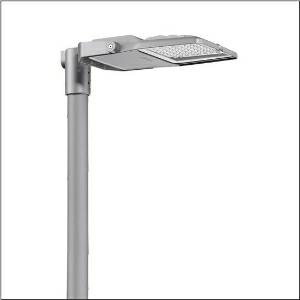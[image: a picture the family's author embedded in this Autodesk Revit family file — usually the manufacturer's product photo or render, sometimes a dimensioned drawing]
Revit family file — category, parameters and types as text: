
# Revit family: floodlight_fl_21_iq_mini___pl64_5xa7771c4e3a_84b6
name_source: partatom
category: Lighting Fixtures
units: mm (PartAtom-declared; Revit-internal decimal feet)

## family parameters
Cut with Voids When Loaded = No
Host = Face
Light Source = No
Part Type = Normal
Room Calculation Point = No
Round Connector Dimension = Use Diameter
Shared = No

## types (1)
- --- (1 x LED, 12280 lm, 87.2 W, 4000K)
    Apparent Load = 87 VA
    CIE Flux Codes = 28 80 98 100 100
    Color Rendering = 70
    Color Temperature = 4000K
    Default Elevation = 1800 mm
    Description = Floodlight FL 21 iQ mini, floodlight, primary light control with lens, of PMMA, primary optical cover: protective disc, of toughened safety glass, transparent, light distribution: PL64, light emission: direct distribution, installation type: surface-mounted, LED, High Power LED, rated luminous flux: 12.280lm, luminous efficacy: 141lm/W, light colour: 740, colour temperature: 4000K, control gear: iQ Comfort/DALI, control: Auto-Match, Temp-Guard, Lumen-Switch, Night-Set, Smart-Wire, Light-Fading, Desk-Remote (wireless, voltage-free reading and setting of iQ features in the workshop via application-optimized NFC function/RFID function), optimised constant luminous flux control (CLO 2.0), with terminal, 6-pole, mains connection: 220..240V, AC, 50/60Hz, start of lifetime: 87W, end of service life: 92W, reduction: 40W, luminaire housing, of diecast aluminium, powder-coated, Siteco® metallic grey (DB 702S), corrosivity category C5 mid according to DIN EN ISO 12944, suitable for swimming pools, chlorine-resistant, sealing non-destructively replaceable, please order mast flange separately, mast bracket, of steel, galvanised, powder-coated, Siteco® metallic grey (DB 702S), protection rating (complete): IP66, insulation class (complete): insulation class II (safety insulation), certification: CE, ENEC, VDE, protection symbol: D, impact resistance: IK08, permissible operating ambient temperature: -40..+40°C, permissible operating ambient temperature for outdoor applications: -40..+50°C, standard: DIN EN 12944, LABS conformity tested according to VDMA 24364:2018-05, packaging unit: 1 piece

Light Distribution: PL64
    Height = 70 mm
    Lamp = 1 x LED
    Lamp Light Flux = 12280 lm
    Lamp Power = 87.2 W
    Lamp count = 1
    Length = 485 mm
    Luminous efficacy = 141 lm/W
    Manufacturer = Siteco
    ModVariant = No
    Model = 5XA7771C4E3A
    Number of Poles = 1
    OnlyDefault = Yes
    Power Factor = 1
    Product Name = Floodlight FL 21 iQ mini | PL64
    Product group = floodlight | pylon annexe
    ProductGroupID = 6201
    Protection Class = Protection class II
    Protection Degree = IP 66
    RLX_Detail_Level = 1
    RLX_Emergency_Light_Flux = 0 lm
    RLX_Emergency_Type = 0
    RLX_Emergency_Type_DB = No
    RlxData = <blob elided: 101333 chars, md5=89fbc040>
    Socket = socket
    Standby Power = 0 W
    System Light Flux = 12280 lm
    System Power = 87 W
    Type Comments = factory setting: luminous flux: 100 % | dim-lin: 254 | 456 mA
    Type Image = l_1007125.jpg
    URL = http://relux.com
    VarID = @adj_187971
    Voltage = 0 V
    Weight = 0.00 kg
    Width = 337 mm

## geometry (parser evidence)
native form markers: Blend x4, Sweep x12
no freeform markers — native parametric forms only
